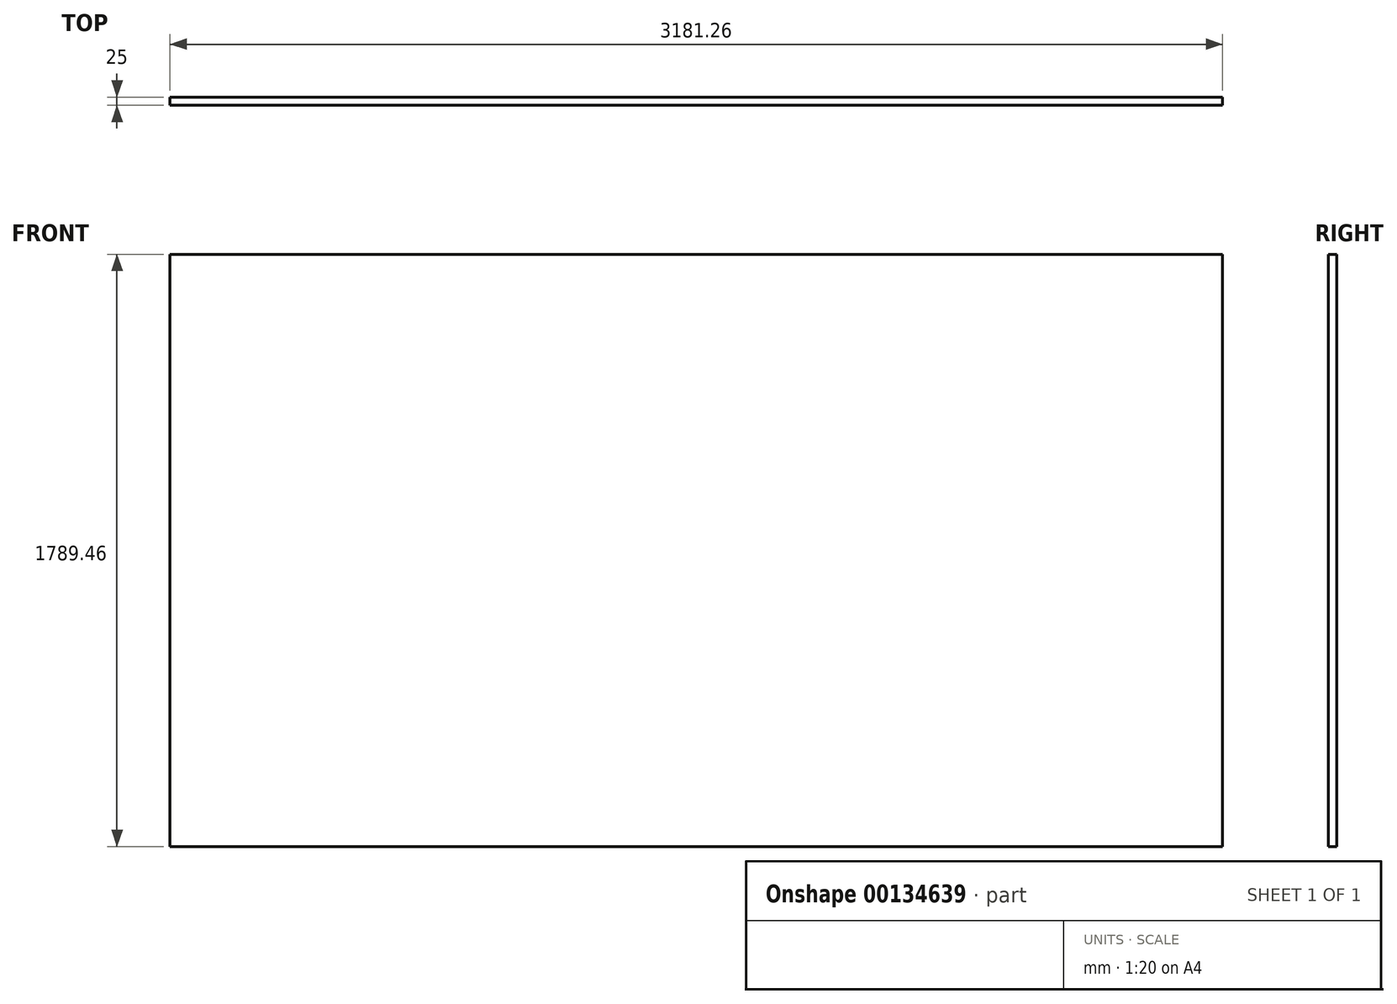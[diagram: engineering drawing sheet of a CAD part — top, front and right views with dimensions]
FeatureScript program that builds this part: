
annotation { "Feature Type Name" : "Feature", "Feature Type Description" : "" }
export const myFeature = defineFeature(function(context is Context, id is Id, definition is map)
    precondition{}
    {
        {
            var Q0;
            Q0=qCreatedBy(makeId("Front.planeOp"),FACE);
            var sketch = newSketch(context, id + "F0", { "sketchPlane" : qUnion([Q0])});
            skLineSegment(sketch, "E0.bottom", {"start": v(1590.63, -894.73) * mm, "end": v(-1590.63, -894.73) * mm});
            skLineSegment(sketch, "E0.top", {"start": v(1590.63, 894.73) * mm, "end": v(-1590.63, 894.73) * mm});
            skLineSegment(sketch, "E0.left", {"start": v(1590.63, -894.73) * mm, "end": v(1590.63, 894.73) * mm});
            skLineSegment(sketch, "E0.right", {"start": v(-1590.63, -894.73) * mm, "end": v(-1590.63, 894.73) * mm});
            skPoint(sketch, "E0.middle", {"position": v(0, 0) * mm});
            skSolve(sketch);
        }
        {
            var Q0;
            Q0=makeQuery(id+"F0.imprint","IMPRINT",FACE,{"disambiguationData":[TD([[makeQuery(id+"F0.imprint","IMPRINT",EDGE,{"derivedFrom":sQuery(id+"F0.wireOp",EDGE,"E0.bottom")}),-1.0]])]});
            extrude(context, id + "F1", {"entities" : qUnion([Q0]), "depth" : 25 * mm});
        }
    });
